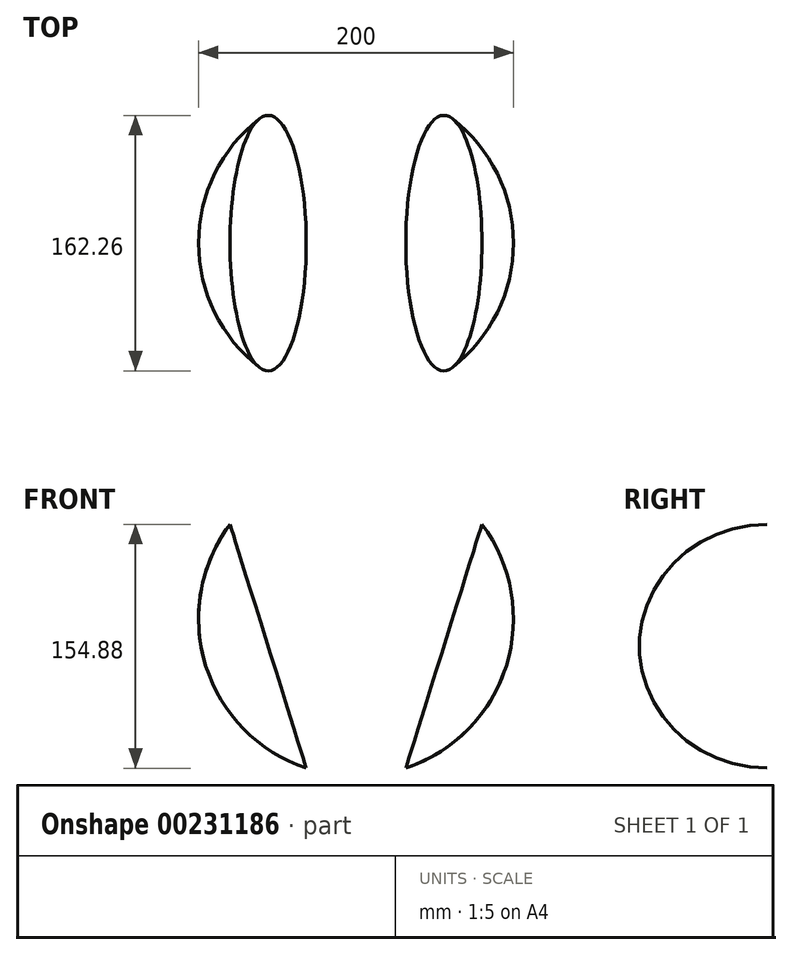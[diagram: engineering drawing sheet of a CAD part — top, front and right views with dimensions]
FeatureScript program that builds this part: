
annotation { "Feature Type Name" : "Feature", "Feature Type Description" : "" }
export const myFeature = defineFeature(function(context is Context, id is Id, definition is map)
    precondition{}
    {
        {
            var Q0;
            Q0=qCreatedBy(makeId("Front.planeOp"),FACE);
            var sketch = newSketch(context, id + "F0", { "sketchPlane" : qUnion([Q0])});
            skCircle(sketch, "E0", {"center": v(0, 0) * mm, "radius": 100 * mm});
            skLineSegment(sketch, "E1", {"start": v(0, 0) * mm, "end": v(0, -100) * mm});
            skLineSegment(sketch, "E2", {"start": v(0, 0) * mm, "end": v(0, 100) * mm});
            skLineSegment(sketch, "E3", {"start": v(0, -100) * mm, "end": v(30, -100) * mm});
            skLineSegment(sketch, "E4", {"start": v(0, -100) * mm, "end": v(-30, -100) * mm});
            skLineSegment(sketch, "E5", {"start": v(0, -100) * mm, "end": v(0, 60) * mm});
            skLineSegment(sketch, "E6", {"start": v(0, 60) * mm, "end": v(80, 60) * mm});
            skLineSegment(sketch, "E7", {"start": v(0, 60) * mm, "end": v(-80, 60) * mm});
            skLineSegment(sketch, "E8", {"start": v(-30, -100) * mm, "end": v(-80, 60) * mm});
            skLineSegment(sketch, "E9", {"start": v(30, -100) * mm, "end": v(80, 60) * mm});
            skLineSegment(sketch, "E10", {"start": v(-31.6, -94.88) * mm, "end": v(-80, 60) * mm});
            skLineSegment(sketch, "E11", {"start": v(31.6, -94.88) * mm, "end": v(80, 60) * mm});
            skLineSegment(sketch, "E12", {"start": v(-31.6, -94.88) * mm, "end": v(31.6, -94.88) * mm});
            skLineSegment(sketch, "E13", {"start": v(-55.8, -17.44) * mm, "end": v(-95.45, -29.83) * mm});
            skLineSegment(sketch, "E14", {"start": v(55.8, -17.44) * mm, "end": v(95.45, -29.83) * mm});
            skLineSegment(sketch, "E15", {"start": v(-55.8, -17.44) * mm, "end": v(-75.62, -23.63) * mm});
            skLineSegment(sketch, "E16", {"start": v(55.8, -17.44) * mm, "end": v(75.62, -23.63) * mm});
            skLineSegment(sketch, "E17", {"start": v(-30, -100) * mm, "end": v(-45, -100) * mm});
            skLineSegment(sketch, "E18", {"start": v(30, -100) * mm, "end": v(50, -100) * mm});
            skLineSegment(sketch, "E19", {"start": v(-55.8, -17.44) * mm, "end": v(-70.12, -21.91) * mm});
            skLineSegment(sketch, "E20", {"start": v(-45, -100) * mm, "end": v(-70.12, -21.91) * mm});
            skLineSegment(sketch, "E21", {"start": v(55.8, -17.44) * mm, "end": v(74.9, -23.4) * mm});
            skLineSegment(sketch, "E22", {"start": v(50, -100) * mm, "end": v(74.9, -23.4) * mm});
            skLineSegment(sketch, "E23", {"start": v(0, 0) * mm, "end": v(100, 0) * mm});
            skLineSegment(sketch, "E24", {"start": v(0, 0) * mm, "end": v(-100, 0) * mm});
            skSolve(sketch);
        }
        {
            var Q0;
            {var subQ1=sQuery(id+"F0.wireOp",EDGE,"E0");var subQ3=sQuery(id+"F0.wireOp",EDGE,"E24");var subQ4=makeQuery(id+"F0.imprint","INTERSECT",VERTEX,{"derivedFrom":[subQ1,subQ3]});Q0=makeQuery(id+"F0.imprint","IMPRINT",FACE,{"disambiguationData":[TD([[makeQuery(id+"F0.imprint","IMPRINT",EDGE,{"disambiguationData":[TD([[subQ4,1.0]])],"derivedFrom":subQ3}),-1.0]])]});}
            var Q1;
            {var subQ0=sQuery(id+"F0.wireOp",EDGE,"E13");Q1=makeQuery(id+"F0.imprint","IMPRINT",FACE,{"disambiguationData":[TD([[makeQuery(id+"F0.imprint","IMPRINT",EDGE,{"derivedFrom":subQ0}),-1.0]])]});}
            var Q2;
            Q2=sQuery(id+"F0.wireOp",EDGE,"E13");
            revolve(context, id + "F1", {"entities" : qUnion([Q0, Q1]), "axis" : qUnion([Q2]), "revolveType" : RevolveType.FULL});
        }
        {
            var Q0;
            {var subQ0=sQuery(id+"F0.wireOp",EDGE,"E14");Q0=makeQuery(id+"F0.imprint","IMPRINT",FACE,{"disambiguationData":[TD([[makeQuery(id+"F0.imprint","IMPRINT",EDGE,{"derivedFrom":subQ0}),1.0]])]});}
            var Q1;
            {var subQ1=sQuery(id+"F0.wireOp",EDGE,"E0");var subQ3=sQuery(id+"F0.wireOp",EDGE,"E23");var subQ4=makeQuery(id+"F0.imprint","INTERSECT",VERTEX,{"derivedFrom":[subQ1,subQ3]});Q1=makeQuery(id+"F0.imprint","IMPRINT",FACE,{"disambiguationData":[TD([[makeQuery(id+"F0.imprint","IMPRINT",EDGE,{"disambiguationData":[TD([[subQ4,1.0]])],"derivedFrom":subQ3}),1.0]])]});}
            var Q2;
            Q2=sQuery(id+"F0.wireOp",EDGE,"E14");
            revolve(context, id + "F2", {"entities" : qUnion([Q0, Q1]), "axis" : qUnion([Q2]), "revolveType" : RevolveType.FULL});
        }
    });
